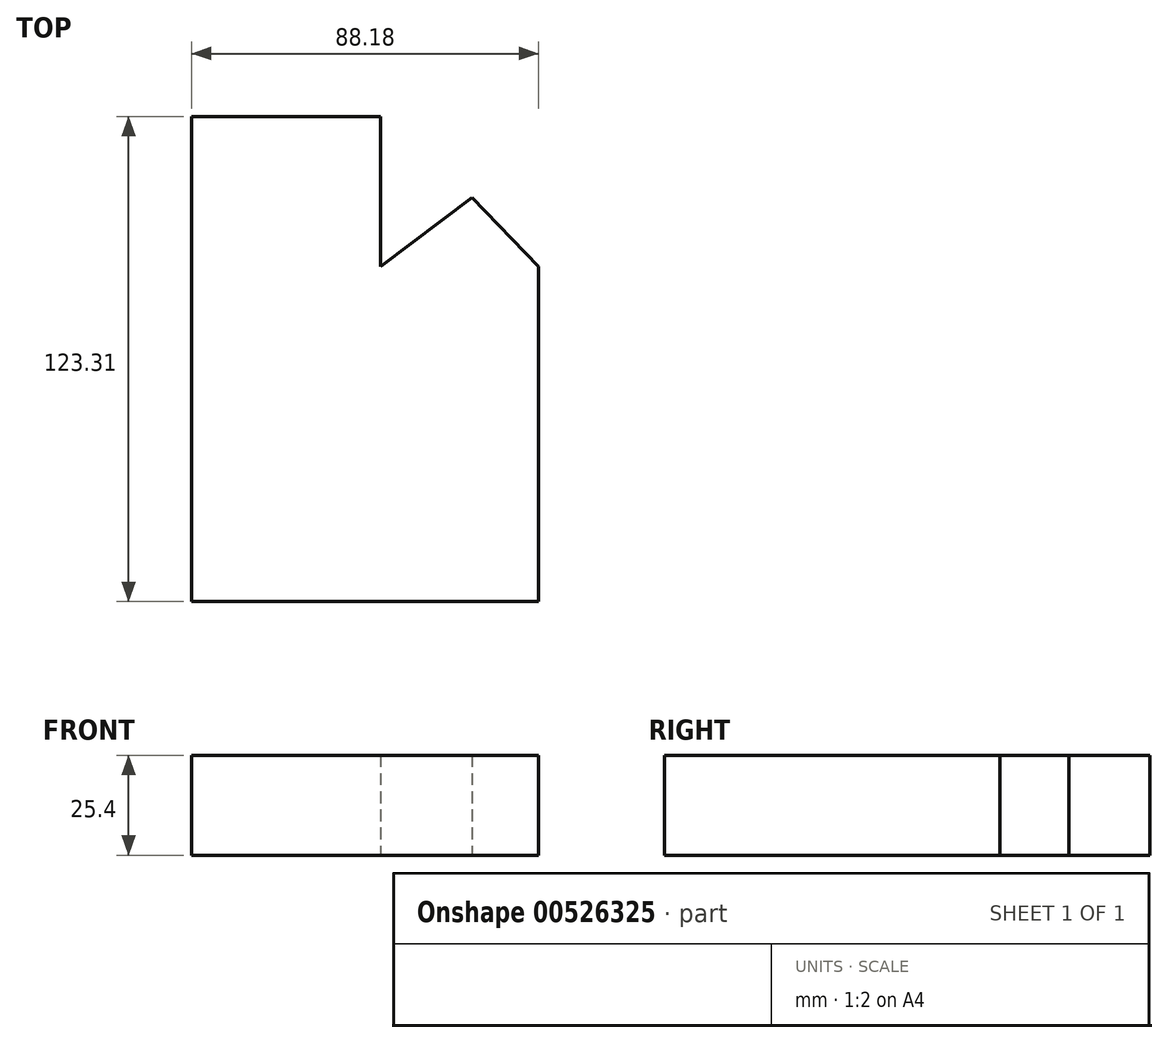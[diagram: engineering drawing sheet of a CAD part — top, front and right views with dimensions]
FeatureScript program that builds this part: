
annotation { "Feature Type Name" : "Feature", "Feature Type Description" : "" }
export const myFeature = defineFeature(function(context is Context, id is Id, definition is map)
    precondition{}
    {
        {
            var Q0;
            Q0=qCreatedBy(makeId("Top.planeOp"),FACE);
            var sketch = newSketch(context, id + "F0", { "sketchPlane" : qUnion([Q0])});
            skLineSegment(sketch, "E0", {"start": v(0, 0) * mm, "end": v(0, -85.17) * mm});
            skLineSegment(sketch, "E1", {"start": v(0, -85.17) * mm, "end": v(-88.18, -85.17) * mm});
            skLineSegment(sketch, "E2", {"start": v(-88.18, -85.17) * mm, "end": v(-88.18, 38.14) * mm});
            skLineSegment(sketch, "E3", {"start": v(-88.18, 38.14) * mm, "end": v(-40.14, 38.14) * mm});
            skLineSegment(sketch, "E4", {"start": v(-40.14, 38.14) * mm, "end": v(-40.14, 0) * mm});
            skLineSegment(sketch, "E5", {"start": v(-40.14, 0) * mm, "end": v(-16.88, 17.57) * mm});
            skLineSegment(sketch, "E6", {"start": v(-16.88, 17.57) * mm, "end": v(0, 0) * mm});
            skSolve(sketch);
        }
        {
            var Q0;
            Q0=makeQuery(id+"F0.imprint","IMPRINT",FACE,{"disambiguationData":[TD([[makeQuery(id+"F0.imprint","IMPRINT",EDGE,{"derivedFrom":sQuery(id+"F0.wireOp",EDGE,"E0")}),-1.0]])]});
            extrude(context, id + "F1", {"entities" : qUnion([Q0]), "depth" : 25.4 * mm, "offsetDistance" : 25.4 * mm});
        }
    });
